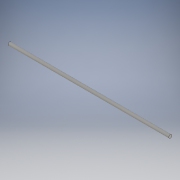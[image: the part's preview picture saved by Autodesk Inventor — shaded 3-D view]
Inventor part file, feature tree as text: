
AUTODESK INVENTOR PART (.ipt)
format: ipt  version: 2018 (Build 220112000, 112)  size: 95,232 bytes
history: native  units: in
note: dims shown in document units (in); Inventor stores cm internally (conversion verified against a paired STEP export)
features: revolve x1, thread x1, sketch x1
ambient origin geometry x8: Origin, YZ Plane, XZ Plane, XY Plane, X Axis, Y Axis, Z Axis, Center Point
bodies: Solid1 (feature_tree)
feature tree (3):
  revolve  "Revolution1"  [1 undecoded]
  thread  "Thread1"  [1 undecoded]
  sketch  "Sketch1"  dims[d0=0.1575in d1=15.748in d2=90.0deg d3=0.3937in d4=0.0in]
note: 2 required parameter values undecoded (feature->parameter linkage not recoverable at this tier; creation-order binding heuristic only, values carry confidence <= 0.55)